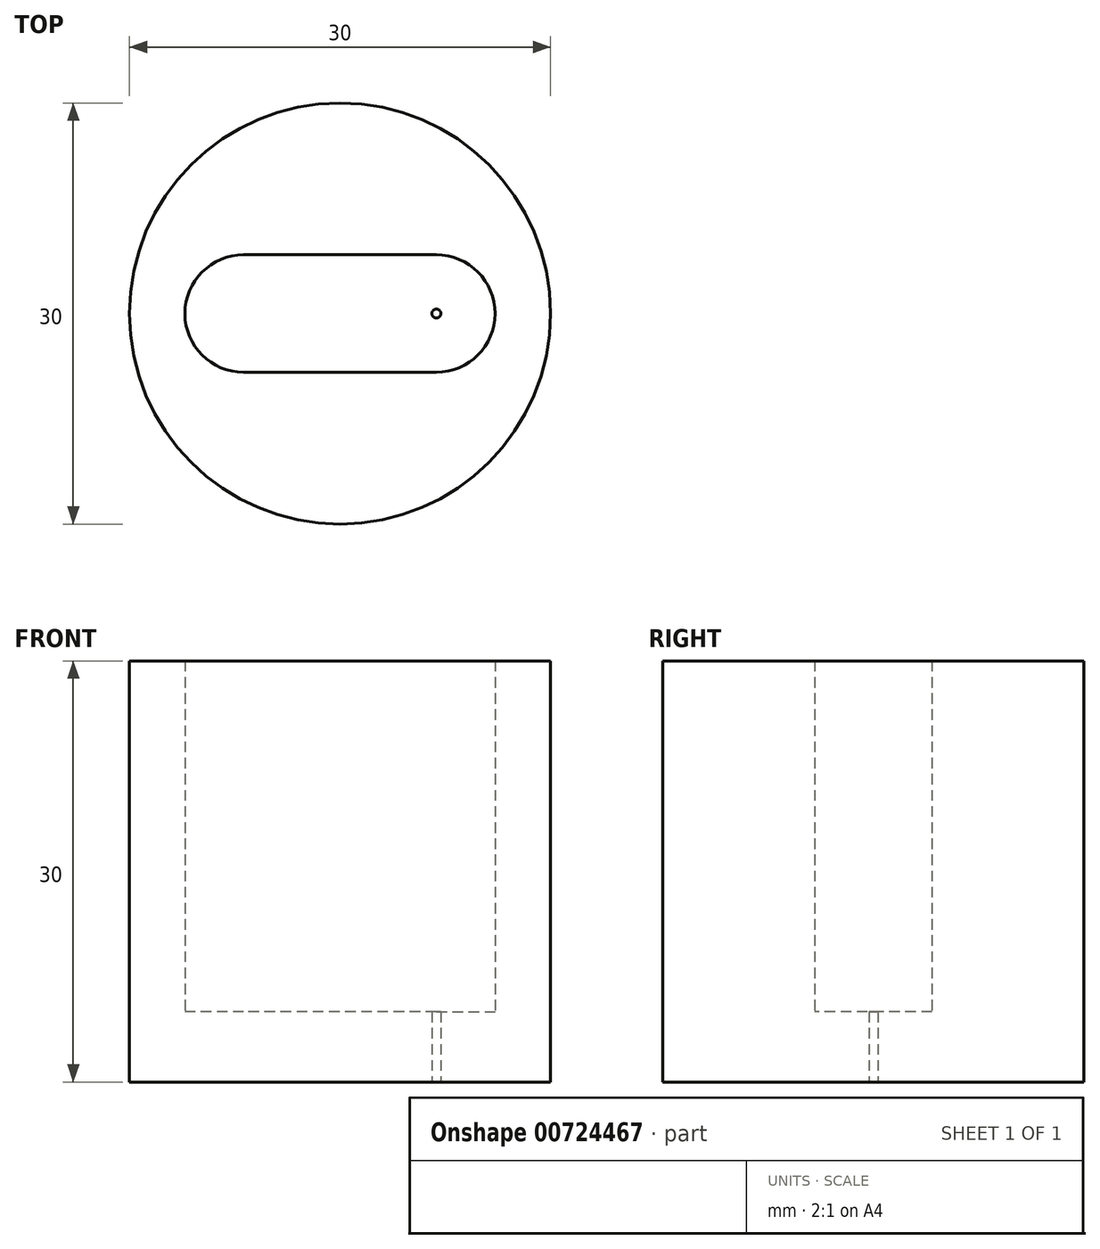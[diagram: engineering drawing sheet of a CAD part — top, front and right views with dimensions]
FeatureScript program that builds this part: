
annotation { "Feature Type Name" : "Feature", "Feature Type Description" : "" }
export const myFeature = defineFeature(function(context is Context, id is Id, definition is map)
    precondition{}
    {
        {
            var Q0;
            Q0=qCreatedBy(makeId("Top.planeOp"),FACE);
            var sketch = newSketch(context, id + "F0", { "sketchPlane" : qUnion([Q0])});
            skCircle(sketch, "E0", {"center": v(0, 0) * mm, "radius": 15 * mm});
            skLineSegment(sketch, "E1.bottom", {"start": v(6.87, 4.18) * mm, "end": v(-6.87, 4.18) * mm});
            skLineSegment(sketch, "E1.top", {"start": v(6.87, -4.18) * mm, "end": v(-6.87, -4.18) * mm});
            skLineSegment(sketch, "E1.left", {"start": v(6.87, 0.32) * mm, "end": v(6.87, -0.32) * mm});
            skCircle(sketch, "E2", {"center": v(6.87, 0) * mm, "radius": 0.32 * mm});
            skArc(sketch, "E3", {"start": v(-6.87, 4.18) * mm, "mid": v(-11.05, 0) * mm, "end": v(-6.87, -4.18) * mm});
            skArc(sketch, "E4", {"start": v(6.87, -4.18) * mm, "mid": v(11.05, 0) * mm, "end": v(6.87, 4.18) * mm});
            skSolve(sketch);
        }
        {
            var Q0;
            Q0=makeQuery(id+"F0.imprint","IMPRINT",FACE,{"disambiguationData":[TD([[makeQuery(id+"F0.imprint","IMPRINT",EDGE,{"derivedFrom":sQuery(id+"F0.wireOp",EDGE,"E0")}),1.0]])]});
            extrude(context, id + "F1", {"entities" : qUnion([Q0]), "depth" : 30 * mm, "offsetDistance" : 25 * mm});
        }
        {
            var Q0;
            Q0=makeQuery(id+"F0.imprint","IMPRINT",FACE,{"disambiguationData":[TD([[makeQuery(id+"F0.imprint","IMPRINT",EDGE,{"derivedFrom":sQuery(id+"F0.wireOp",EDGE,"E1.bottom")}),1.0]])]});
            extrude(context, id + "F2", {"entities" : qUnion([Q0]), "operationType" : NewBodyOperationType.ADD, "depth" : 5 * mm, "offsetDistance" : 25 * mm});
        }
    });
